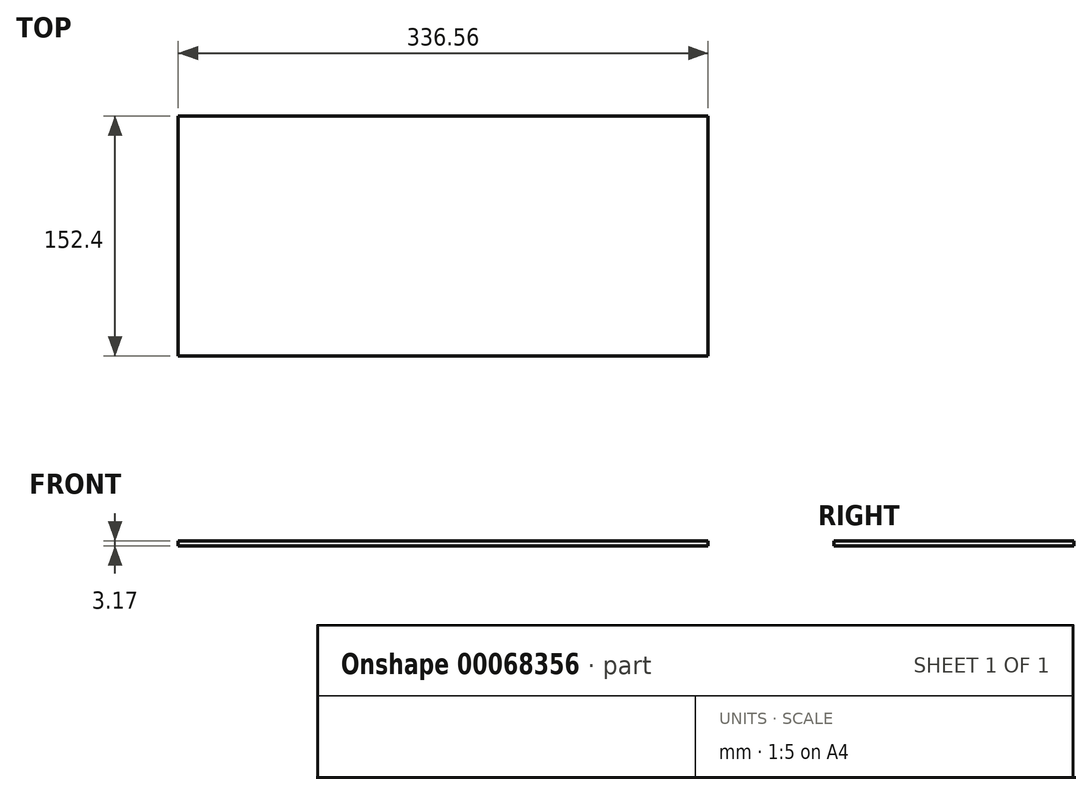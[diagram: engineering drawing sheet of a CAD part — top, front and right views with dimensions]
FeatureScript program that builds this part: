
annotation { "Feature Type Name" : "Feature", "Feature Type Description" : "" }
export const myFeature = defineFeature(function(context is Context, id is Id, definition is map)
    precondition{}
    {
        {
            var Q0;
            Q0=qCreatedBy(makeId("Top.planeOp"),FACE);
            var sketch = newSketch(context, id + "F0", { "sketchPlane" : qUnion([Q0])});
            skLineSegment(sketch, "E0.bottom", {"start": v(168.28, -76.2) * mm, "end": v(-168.28, -76.2) * mm});
            skLineSegment(sketch, "E0.top", {"start": v(168.28, 76.2) * mm, "end": v(-168.28, 76.2) * mm});
            skLineSegment(sketch, "E0.left", {"start": v(168.28, -76.2) * mm, "end": v(168.28, 76.2) * mm});
            skLineSegment(sketch, "E0.right", {"start": v(-168.28, -76.2) * mm, "end": v(-168.28, 76.2) * mm});
            skPoint(sketch, "E0.middle", {"position": v(0, 0) * mm});
            skSolve(sketch);
        }
        {
            var Q0;
            Q0=makeQuery(id+"F0.imprint","IMPRINT",FACE,{"disambiguationData":[TD([[makeQuery(id+"F0.imprint","IMPRINT",EDGE,{"derivedFrom":sQuery(id+"F0.wireOp",EDGE,"E0.bottom")}),-1.0]])]});
            extrude(context, id + "F1", {"entities" : qUnion([Q0]), "depth" : 3.17 * mm});
        }
    });
